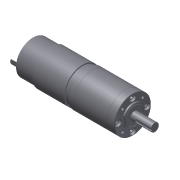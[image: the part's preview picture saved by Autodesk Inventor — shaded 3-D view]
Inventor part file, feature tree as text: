
AUTODESK INVENTOR PART (.ipt)
format: ipt  version: 2011 (Build 150239000, 239)  size: 339,968 bytes
history: native  units: in
note: dims shown in document units (in); Inventor stores cm internally (conversion verified against a paired STEP export)
features: mirror x1, imported_body x1
ambient origin geometry x8: Origin, YZ Plane, XZ Plane, XY Plane, X Axis, Y Axis, Z Axis, Center Point
feature tree (2):
  mirror  "Mirror2"
  imported_body  "Base1"
